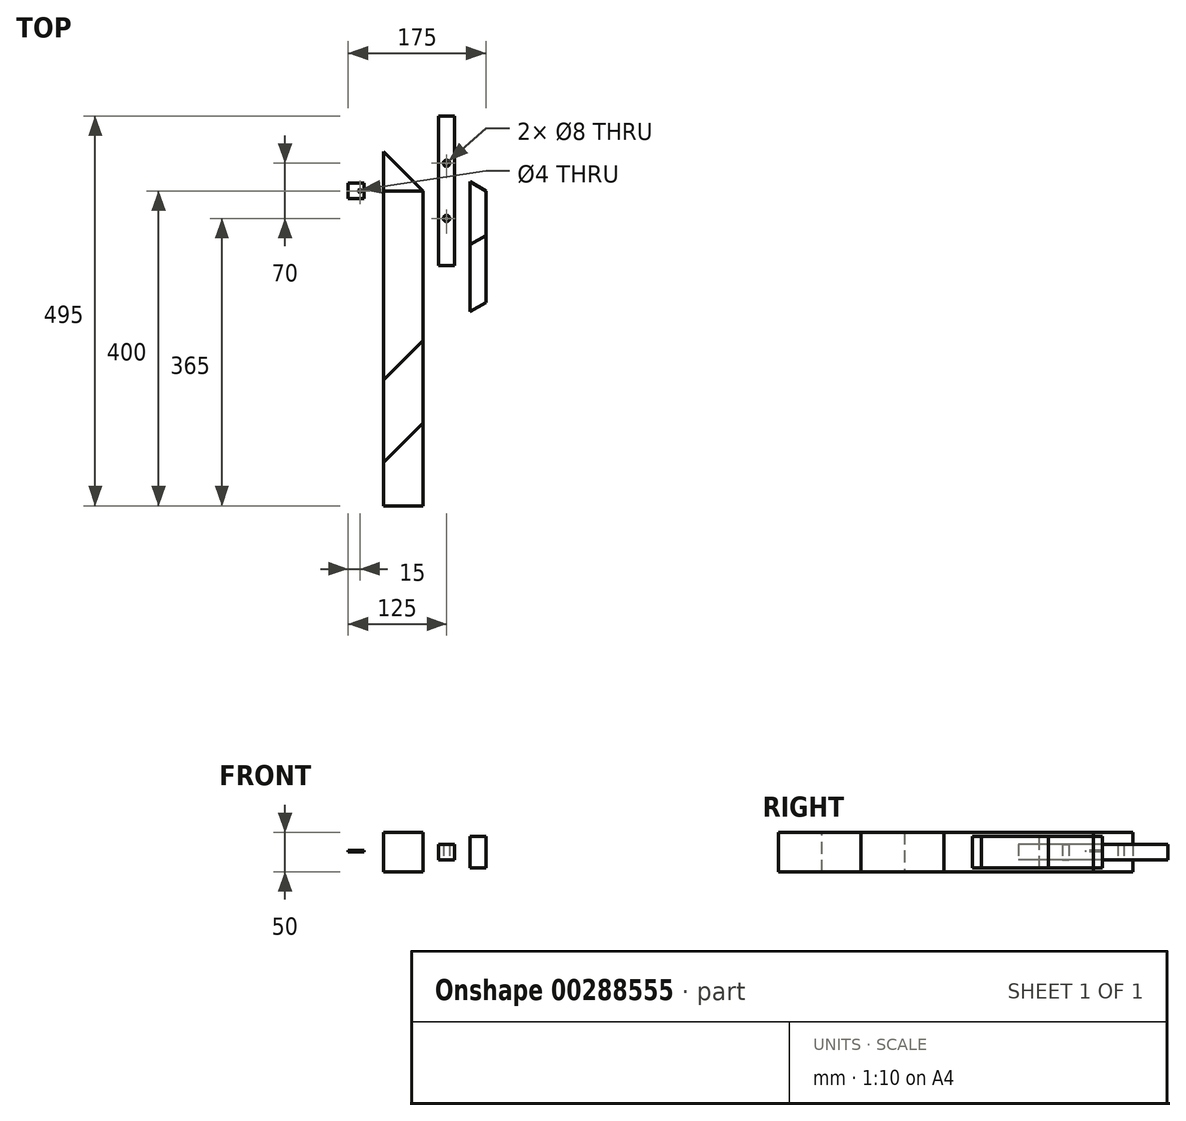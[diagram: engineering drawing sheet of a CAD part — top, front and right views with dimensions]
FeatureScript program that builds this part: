
annotation { "Feature Type Name" : "Feature", "Feature Type Description" : "" }
export const myFeature = defineFeature(function(context is Context, id is Id, definition is map)
    precondition{}
    {
        {
            assignVariable(context, id + "F0", {"variableType" : VariableType.LENGTH, "name" : "w", "lengthValue" : 290 * mm});
        }
        {
            assignVariable(context, id + "F1", {"variableType" : VariableType.LENGTH, "name" : "d", "lengthValue" : 395 * mm});
        }
        {
            assignVariable(context, id + "F2", {"variableType" : VariableType.LENGTH, "name" : "h", "lengthValue" : 500 * mm});
        }
        {
            assignVariable(context, id + "F3", {"variableType" : VariableType.LENGTH, "name" : "tube", "lengthValue" : 50 * mm});
        }
        {
            var Q0;
            Q0=qCreatedBy(makeId("Front.planeOp"),FACE);
            var sketch = newSketch(context, id + "F4", { "sketchPlane" : qUnion([Q0])});
            skLineSegment(sketch, "E0.bottom", {"start": v(-25, 25) * mm, "end": v(25, 25) * mm});
            skLineSegment(sketch, "E0.top", {"start": v(-25, -25) * mm, "end": v(25, -25) * mm});
            skLineSegment(sketch, "E0.left", {"start": v(-25, 25) * mm, "end": v(-25, -25) * mm});
            skLineSegment(sketch, "E0.right", {"start": v(25, 25) * mm, "end": v(25, -25) * mm});
            skLineSegment(sketch, "E1", {"start": v(-25, 0) * mm, "end": v(25, 0) * mm, "construction": true});
            skLineSegment(sketch, "E2", {"start": v(25, 0) * mm, "end": v(65, 0) * mm, "construction": true});
            skLineSegment(sketch, "E3.bottom", {"start": v(45, 10) * mm, "end": v(65, 10) * mm});
            skLineSegment(sketch, "E3.top", {"start": v(45, -10) * mm, "end": v(65, -10) * mm});
            skLineSegment(sketch, "E3.left", {"start": v(45, 10) * mm, "end": v(45, -10) * mm});
            skLineSegment(sketch, "E3.right", {"start": v(65, 10) * mm, "end": v(65, -10) * mm});
            skPoint(sketch, "E4", {"position": v(45, 0) * mm});
            skLineSegment(sketch, "E5", {"start": v(65, 0) * mm, "end": v(105, 0) * mm, "construction": true});
            skLineSegment(sketch, "E6.bottom", {"start": v(85, 20) * mm, "end": v(105, 20) * mm});
            skLineSegment(sketch, "E6.top", {"start": v(85, -20) * mm, "end": v(105, -20) * mm});
            skLineSegment(sketch, "E6.left", {"start": v(85, 20) * mm, "end": v(85, -20) * mm});
            skLineSegment(sketch, "E6.right", {"start": v(105, 20) * mm, "end": v(105, -20) * mm});
            skPoint(sketch, "E7", {"position": v(85, 0) * mm});
            skSolve(sketch);
        }
        {
            var Q0;
            Q0=qCreatedBy(makeId("Top.planeOp"),FACE);
            var sketch = newSketch(context, id + "F5", { "sketchPlane" : qUnion([Q0])});
            skLineSegment(sketch, "E8.0", {"start": v(-25, 0) * mm, "end": v(25, 0) * mm});
            skLineSegment(sketch, "E9", {"start": v(25, 0) * mm, "end": v(-25, 50) * mm});
            skLineSegment(sketch, "E10", {"start": v(25, -190) * mm, "end": v(-25, -240) * mm});
            skLineSegment(sketch, "E11", {"start": v(25, -295) * mm, "end": v(-25, -345) * mm});
            skLineSegment(sketch, "E12", {"start": v(25, -400) * mm, "end": v(-25, -400) * mm});
            skSolve(sketch);
        }
        {
            var Q0;
            Q0=sQuery(id+"F5.wireOp",EDGE,"E9");
            cPlane(context, id + "F6", {"entities" : qUnion([Q0]), "cplaneType" : CPlaneType.LINE_ANGLE, "offset" : 25 * mm, "angle" : 90 * degree, "width" : 150 * mm, "height" : 150 * mm});
        }
        {
            var Q0;
            Q0=sQuery(id+"F5.wireOp",EDGE,"E10");
            cPlane(context, id + "F7", {"entities" : qUnion([Q0]), "cplaneType" : CPlaneType.LINE_ANGLE, "offset" : 25 * mm, "angle" : 90 * degree, "width" : 150 * mm, "height" : 150 * mm});
        }
        {
            var Q0;
            Q0=sQuery(id+"F5.wireOp",EDGE,"E11");
            cPlane(context, id + "F8", {"entities" : qUnion([Q0]), "cplaneType" : CPlaneType.LINE_ANGLE, "offset" : 25 * mm, "angle" : 90 * degree, "width" : 150 * mm, "height" : 150 * mm});
        }
        {
            var Q0;
            Q0=makeQuery(id+"F4.imprint","IMPRINT",FACE,{"disambiguationData":[TD([[makeQuery(id+"F4.imprint","IMPRINT",EDGE,{"derivedFrom":sQuery(id+"F4.wireOp",EDGE,"E0.bottom")}),-1.0]])]});
            var Q1;
            Q1=qCreatedBy(id+"F7.planeOp",FACE);
            var Q2;
            Q2=qCreatedBy(id+"F6.planeOp",FACE);
            extrude(context, id + "F9", {"entities" : qUnion([Q0]), "endBound" : BoundingType.UP_TO_SURFACE, "depth" : getVariable(context, 'w') - 2 * getVariable(context, 'tube'), "endBoundEntityFace" : qUnion([Q1]), "offsetDistance" : 25 * mm, "hasSecondDirection" : true, "secondDirectionBound" : BoundingType.UP_TO_SURFACE, "secondDirectionOppositeDirection" : true, "secondDirectionDepth" : 25 * mm, "secondDirectionBoundEntityFace" : qUnion([Q2])});
        }
        {
            var Q0;
            Q0=makeQuery(id+"F4.imprint","IMPRINT",FACE,{"disambiguationData":[TD([[makeQuery(id+"F4.imprint","IMPRINT",EDGE,{"derivedFrom":sQuery(id+"F4.wireOp",EDGE,"E0.bottom")}),-1.0]])]});
            var Q1;
            Q1=qCreatedBy(id+"F6.planeOp",FACE);
            var Q2;
            Q2=qCreatedBy(id+"F8.planeOp",FACE);
            extrude(context, id + "F10", {"entities" : qUnion([Q0]), "endBound" : BoundingType.UP_TO_SURFACE, "oppositeDirection" : true, "depth" : getVariable(context, 'd'), "endBoundEntityFace" : qUnion([Q1]), "offsetDistance" : 25 * mm, "hasSecondDirection" : true, "secondDirectionBound" : BoundingType.UP_TO_SURFACE, "secondDirectionOppositeDirection" : false, "secondDirectionDepth" : 25 * mm, "secondDirectionBoundEntityFace" : qUnion([Q2])});
        }
        {
            var Q0;
            Q0=makeQuery(id+"F4.imprint","IMPRINT",FACE,{"disambiguationData":[TD([[makeQuery(id+"F4.imprint","IMPRINT",EDGE,{"derivedFrom":sQuery(id+"F4.wireOp",EDGE,"E0.bottom")}),-1.0]])]});
            var Q1;
            Q1=sQuery(id+"F5.wireOp",VERTEX,"E12.end");
            extrude(context, id + "F11", {"entities" : qUnion([Q0]), "endBound" : BoundingType.UP_TO_VERTEX, "depth" : getVariable(context, 'h') - 2 * getVariable(context, 'tube'), "endBoundEntityVertex" : qUnion([Q1]), "offsetDistance" : 25 * mm});
        }
        {
            var Q0;
            Q0=qCreatedBy(makeId("Top.planeOp"),FACE);
            var sketch = newSketch(context, id + "F12", { "sketchPlane" : qUnion([Q0])});
            skLineSegment(sketch, "E13.0", {"start": v(45, 0) * mm, "end": v(65, 0) * mm, "construction": true});
            skLineSegment(sketch, "E14.bottom", {"start": v(45, -95) * mm, "end": v(65, -95) * mm});
            skLineSegment(sketch, "E14.top", {"start": v(45, 95) * mm, "end": v(65, 95) * mm});
            skLineSegment(sketch, "E14.left", {"start": v(45, 95) * mm, "end": v(45, -95) * mm});
            skLineSegment(sketch, "E14.right", {"start": v(65, 95) * mm, "end": v(65, -95) * mm});
            skCircle(sketch, "E15", {"center": v(55, 35) * mm, "radius": 4 * mm});
            skCircle(sketch, "E16", {"center": v(55, -35) * mm, "radius": 4 * mm});
            skLineSegment(sketch, "E17", {"start": v(55, 35) * mm, "end": v(55, -35) * mm, "construction": true});
            skPoint(sketch, "E18", {"position": v(55, 0) * mm});
            skSolve(sketch);
        }
        {
            var Q0;
            Q0=makeQuery(id+"F12.imprint","IMPRINT",FACE,{"disambiguationData":[TD([[makeQuery(id+"F12.imprint","IMPRINT",EDGE,{"derivedFrom":sQuery(id+"F12.wireOp",EDGE,"E14.bottom")}),1.0]])]});
            var Q1;
            Q1=sQuery(id+"F4.wireOp",VERTEX,"E3.bottom.start");
            var Q2;
            Q2=sQuery(id+"F4.wireOp",VERTEX,"E3.top.start");
            extrude(context, id + "F13", {"entities" : qUnion([Q0]), "endBound" : BoundingType.UP_TO_VERTEX, "depth" : 25 * mm, "endBoundEntityVertex" : qUnion([Q1]), "offsetDistance" : 25 * mm, "hasSecondDirection" : true, "secondDirectionBound" : BoundingType.UP_TO_VERTEX, "secondDirectionOppositeDirection" : true, "secondDirectionDepth" : 25 * mm, "secondDirectionBoundEntityVertex" : qUnion([Q2])});
        }
        {
            var Q0;
            Q0=qCreatedBy(makeId("Top.planeOp"),FACE);
            var sketch = newSketch(context, id + "F14", { "sketchPlane" : qUnion([Q0])});
            skLineSegment(sketch, "E19.0", {"start": v(85, 0) * mm, "end": v(105, 0) * mm});
            skLineSegment(sketch, "E20", {"start": v(105, 0) * mm, "end": v(85, 11.55) * mm});
            skLineSegment(sketch, "E21", {"start": v(105, -56.9) * mm, "end": v(85, -68.45) * mm});
            skLineSegment(sketch, "E22", {"start": v(105, -141.9) * mm, "end": v(85, -153.45) * mm});
            skSolve(sketch);
        }
        {
            var Q0;
            Q0=sQuery(id+"F14.wireOp",EDGE,"E20");
            cPlane(context, id + "F15", {"entities" : qUnion([Q0]), "cplaneType" : CPlaneType.LINE_ANGLE, "offset" : 25 * mm, "angle" : 0 * degree, "width" : 150 * mm, "height" : 150 * mm});
        }
        {
            var Q0;
            Q0=sQuery(id+"F14.wireOp",EDGE,"E21");
            cPlane(context, id + "F16", {"entities" : qUnion([Q0]), "cplaneType" : CPlaneType.LINE_ANGLE, "offset" : 25 * mm, "angle" : 0 * degree, "width" : 150 * mm, "height" : 150 * mm});
        }
        {
            var Q0;
            Q0=sQuery(id+"F14.wireOp",EDGE,"E22");
            cPlane(context, id + "F17", {"entities" : qUnion([Q0]), "cplaneType" : CPlaneType.LINE_ANGLE, "offset" : 25 * mm, "angle" : 0 * degree, "width" : 150 * mm, "height" : 150 * mm});
        }
        {
            var Q0;
            Q0=makeQuery(id+"F4.imprint","IMPRINT",FACE,{"disambiguationData":[TD([[makeQuery(id+"F4.imprint","IMPRINT",EDGE,{"derivedFrom":sQuery(id+"F4.wireOp",EDGE,"E6.bottom")}),-1.0]])]});
            var Q1;
            Q1=qCreatedBy(id+"F15.planeOp",FACE);
            var Q2;
            Q2=qCreatedBy(id+"F16.planeOp",FACE);
            extrude(context, id + "F18", {"entities" : qUnion([Q0]), "endBound" : BoundingType.UP_TO_SURFACE, "oppositeDirection" : true, "depth" : 25 * mm, "endBoundEntityFace" : qUnion([Q1]), "offsetDistance" : 25 * mm, "hasSecondDirection" : true, "secondDirectionBound" : BoundingType.UP_TO_SURFACE, "secondDirectionOppositeDirection" : false, "secondDirectionDepth" : 25 * mm, "secondDirectionBoundEntityFace" : qUnion([Q2])});
        }
        {
            var Q0;
            Q0=makeQuery(id+"F4.imprint","IMPRINT",FACE,{"disambiguationData":[TD([[makeQuery(id+"F4.imprint","IMPRINT",EDGE,{"derivedFrom":sQuery(id+"F4.wireOp",EDGE,"E6.bottom")}),-1.0]])]});
            var Q1;
            Q1=qCreatedBy(id+"F15.planeOp",FACE);
            var Q2;
            Q2=qCreatedBy(id+"F17.planeOp",FACE);
            extrude(context, id + "F19", {"entities" : qUnion([Q0]), "endBound" : BoundingType.UP_TO_SURFACE, "oppositeDirection" : true, "depth" : 25 * mm, "endBoundEntityFace" : qUnion([Q1]), "offsetDistance" : 25 * mm, "hasSecondDirection" : true, "secondDirectionBound" : BoundingType.UP_TO_SURFACE, "secondDirectionOppositeDirection" : false, "secondDirectionDepth" : 25 * mm, "secondDirectionBoundEntityFace" : qUnion([Q2])});
        }
        {
            var Q0;
            Q0=qCreatedBy(makeId("Top.planeOp"),FACE);
            var sketch = newSketch(context, id + "F20", { "sketchPlane" : qUnion([Q0])});
            skLineSegment(sketch, "E23.bottom", {"start": v(-70, -10) * mm, "end": v(-50, -10) * mm});
            skLineSegment(sketch, "E23.top", {"start": v(-70, 10) * mm, "end": v(-50, 10) * mm});
            skLineSegment(sketch, "E23.left", {"start": v(-70, 10) * mm, "end": v(-70, -10) * mm});
            skLineSegment(sketch, "E23.right", {"start": v(-50, 10) * mm, "end": v(-50, -10) * mm});
            skLineSegment(sketch, "E24", {"start": v(0, 0) * mm, "end": v(-50, 0) * mm, "construction": true});
            skCircle(sketch, "E25", {"center": v(-55, 0) * mm, "radius": 2 * mm});
            skSolve(sketch);
        }
        {
            var Q0;
            Q0=makeQuery(id+"F20.imprint","IMPRINT",FACE,{"disambiguationData":[TD([[makeQuery(id+"F20.imprint","IMPRINT",EDGE,{"derivedFrom":sQuery(id+"F20.wireOp",EDGE,"E23.bottom")}),1.0]])]});
            extrude(context, id + "F21", {"entities" : qUnion([Q0]), "depth" : 2 * mm, "offsetDistance" : 25 * mm});
        }
    });
